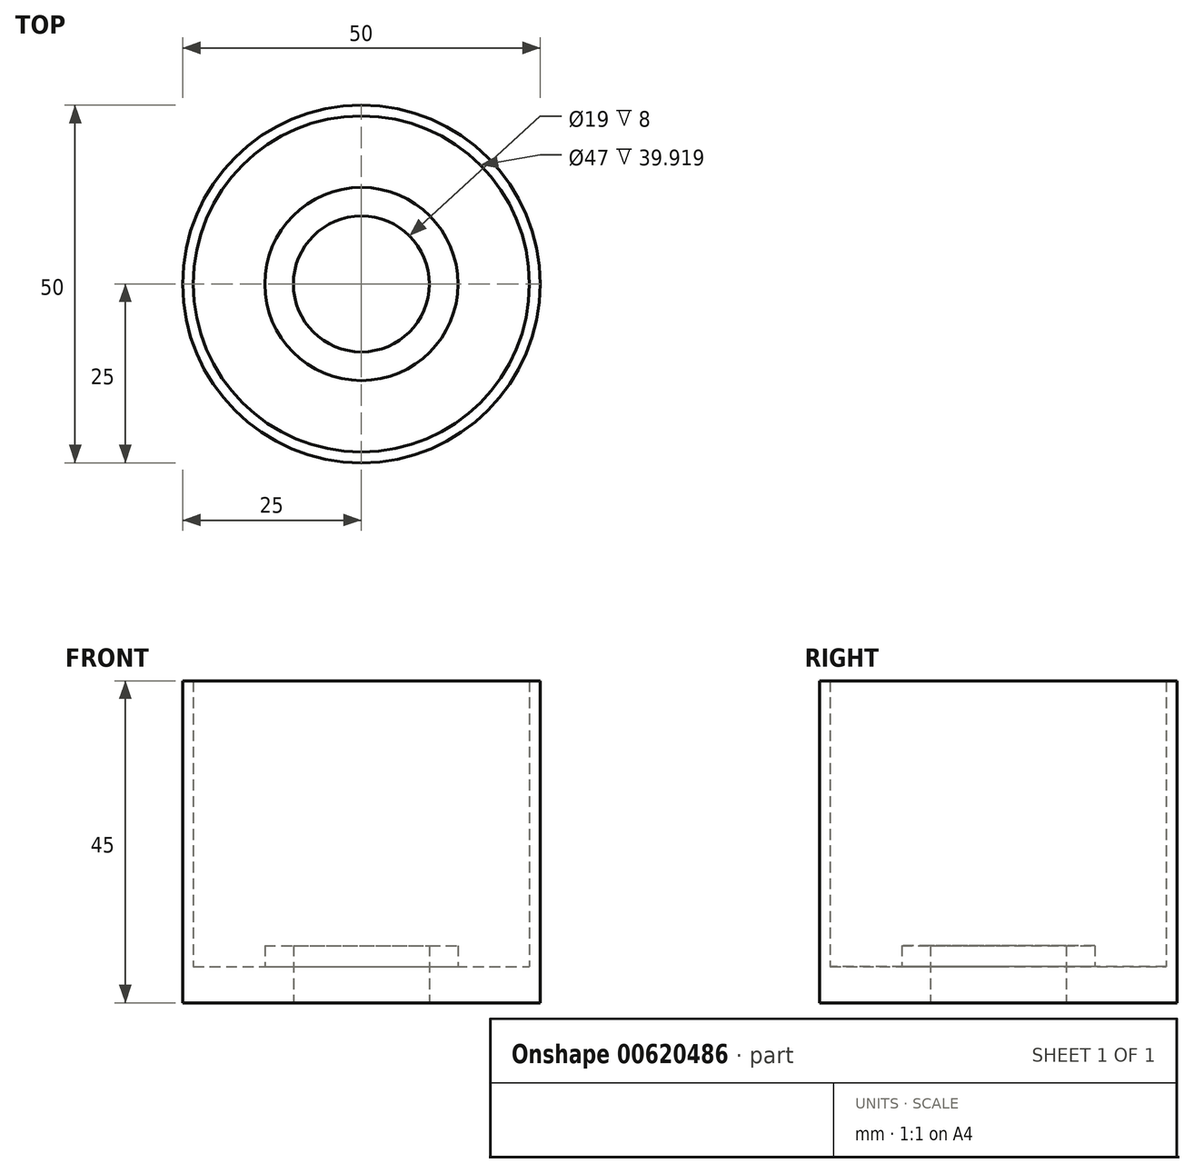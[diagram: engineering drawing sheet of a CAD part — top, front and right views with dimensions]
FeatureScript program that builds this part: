
annotation { "Feature Type Name" : "Feature", "Feature Type Description" : "" }
export const myFeature = defineFeature(function(context is Context, id is Id, definition is map)
    precondition{}
    {
        {
            var Q0;
            Q0=qCreatedBy(makeId("Front.planeOp"),FACE);
            var sketch = newSketch(context, id + "F0", { "sketchPlane" : qUnion([Q0])});
            skLineSegment(sketch, "E0", {"start": v(0, 0) * mm, "end": v(0, 44.2) * mm, "construction": true});
            skLineSegment(sketch, "E1", {"start": v(0, 0) * mm, "end": v(9.5, 0) * mm, "construction": true});
            skLineSegment(sketch, "E2", {"start": v(9.5, 0) * mm, "end": v(9.5, 8) * mm});
            skLineSegment(sketch, "E3", {"start": v(9.5, 8) * mm, "end": v(13.5, 8) * mm});
            skLineSegment(sketch, "E4", {"start": v(13.5, 8) * mm, "end": v(13.5, 5.08) * mm});
            skLineSegment(sketch, "E5", {"start": v(13.5, 5.08) * mm, "end": v(23.5, 5.08) * mm});
            skLineSegment(sketch, "E6", {"start": v(23.5, 5.08) * mm, "end": v(23.5, 45) * mm});
            skLineSegment(sketch, "E7", {"start": v(23.5, 45) * mm, "end": v(25, 45) * mm});
            skLineSegment(sketch, "E8", {"start": v(25, 45) * mm, "end": v(25, 0) * mm});
            skLineSegment(sketch, "E9", {"start": v(25, 0) * mm, "end": v(9.5, 0) * mm});
            skSolve(sketch);
        }
        {
            var Q0;
            Q0=makeQuery(id+"F0.imprint","IMPRINT",FACE,{"disambiguationData":[TD([[makeQuery(id+"F0.imprint","IMPRINT",EDGE,{"derivedFrom":sQuery(id+"F0.wireOp",EDGE,"E2")}),-1.0]])]});
            var Q1;
            Q1=sQuery(id+"F0.wireOp",EDGE,"E0");
            revolve(context, id + "F1", {"entities" : qUnion([Q0]), "axis" : qUnion([Q1]), "revolveType" : RevolveType.FULL});
        }
    });
